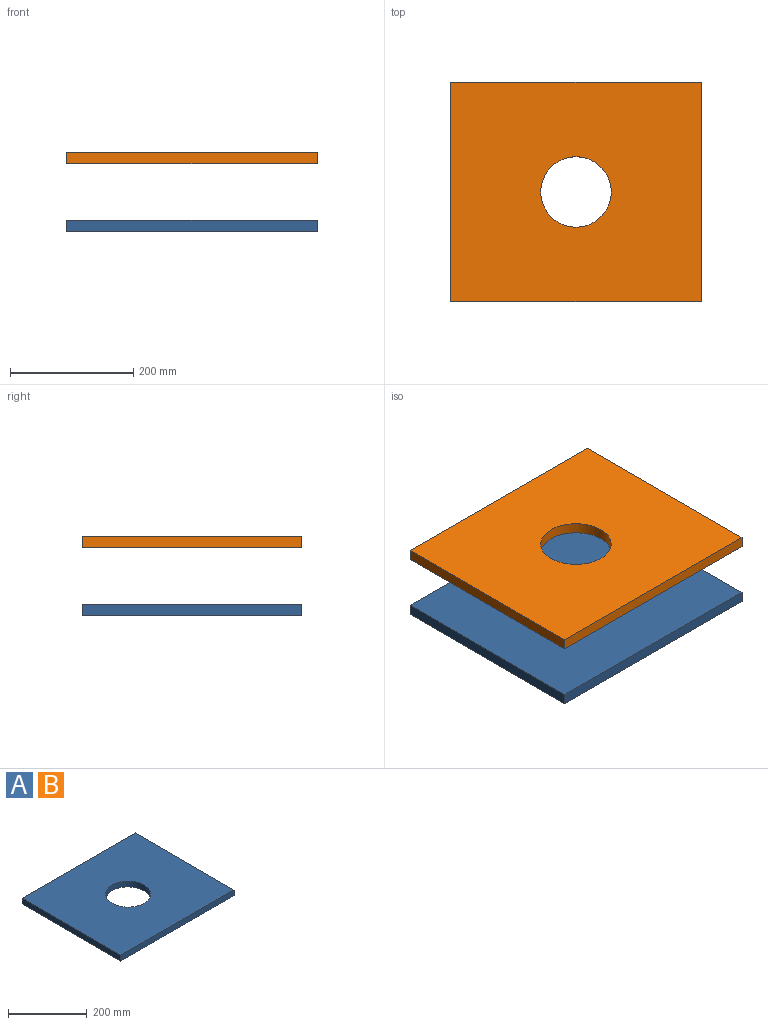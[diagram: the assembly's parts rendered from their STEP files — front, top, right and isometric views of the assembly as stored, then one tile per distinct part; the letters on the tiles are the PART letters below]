
ASSEMBLY  parts=2 mates=3
PART A: 7 faces, bbox 406.4x355.6x18 mm
  f0: plane 355.6x18mm, normal (1,0,0), area 6400.8mm2, adj f1,f3,f5,f6
  f1: plane 406.4x18mm, normal (0,1,0), area 7315.2mm2, adj f0,f2,f5,f6
  f2: plane 355.6x18mm, normal (-1,0,0), area 6400.8mm2, adj f1,f3,f5,f6
  f3: plane 406.4x18mm, normal (0,-1,0), area 7315.2mm2, adj f0,f2,f5,f6
  f4: cylinder r=57.15mm len=114.3mm, axis (0,0,-1), area 6463.5mm2, adj f5,f6
  f5: plane 406.4x355.6mm, normal (0,0,1), area 134255mm2, adj f0,f1,f2,f3,f4
  f6: plane 406.4x355.6mm, normal (0,0,-1), area 134255mm2, adj f0,f1,f2,f3,f4
PART B: same geometry as A
PLACE A t=(86.64,407.33,166.59)mm
PLACE B t=(86.64,407.33,275.59)mm
MATE parallel B.f4 <-> A.f4  axis (0,0,1) through (86.64,407.33,293.59)mm
MATE planar A.f2 <-> B.f2  axis (-1,0,0) through (-116.56,407.33,175.59)mm
MATE planar B.f3 <-> A.f3  axis (0,-1,0) through (86.64,229.53,284.59)mm
